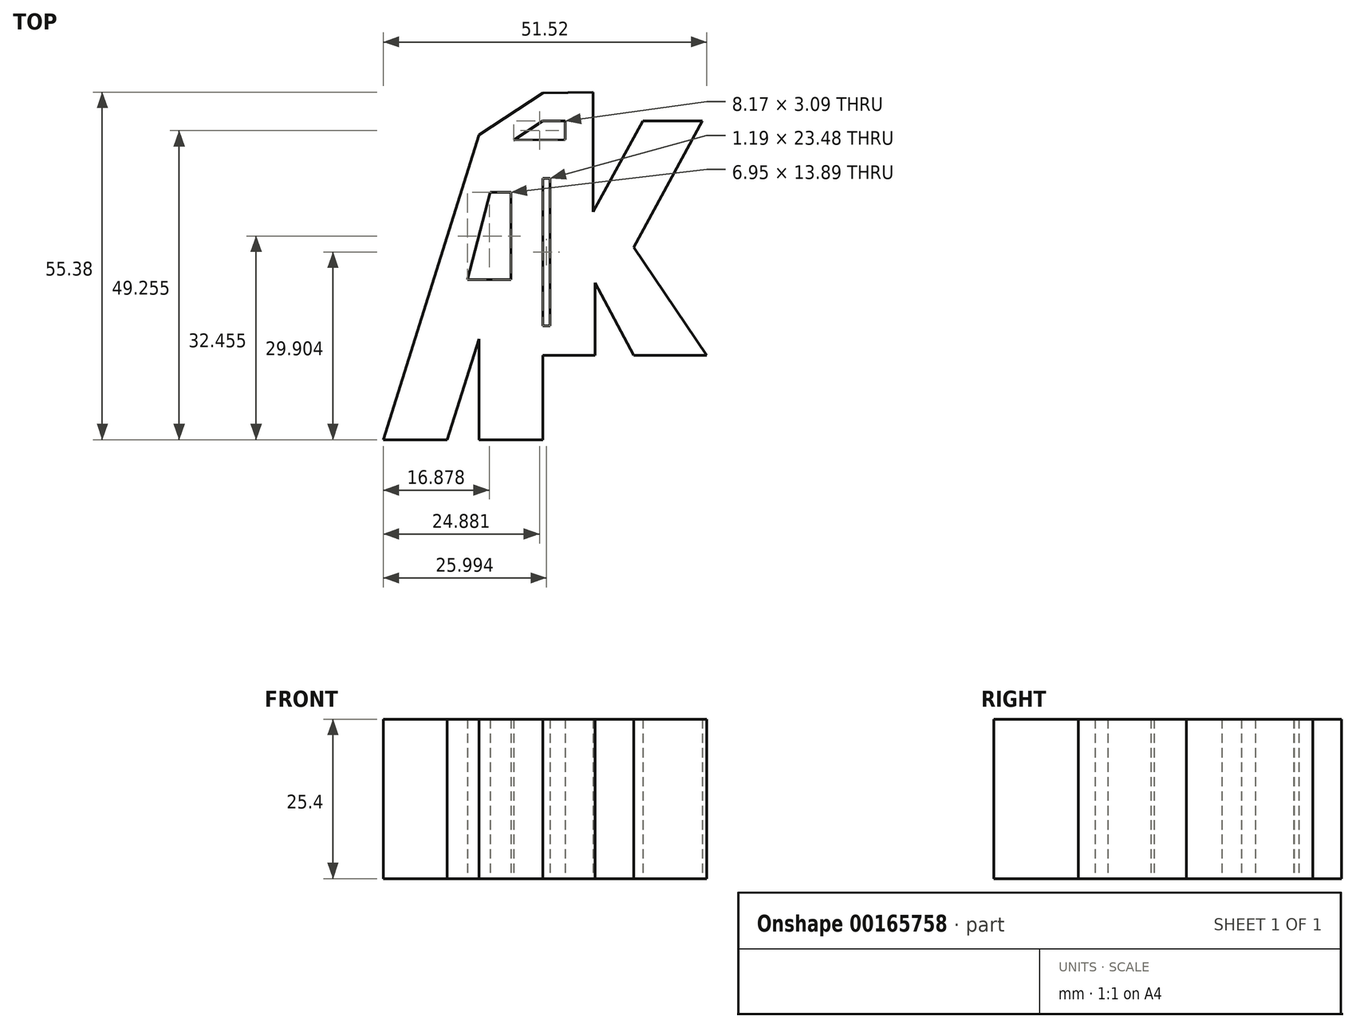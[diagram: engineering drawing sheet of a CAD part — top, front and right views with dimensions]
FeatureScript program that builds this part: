
annotation { "Feature Type Name" : "Feature", "Feature Type Description" : "" }
export const myFeature = defineFeature(function(context is Context, id is Id, definition is map)
    precondition{}
    {
        {
            var Q0;
            Q0=qCreatedBy(makeId("Top.planeOp"),FACE);
            var sketch = newSketch(context, id + "F0", { "sketchPlane" : qUnion([Q0])});
            skLineSegment(sketch, "E0", {"start": v(0, 0) * mm, "end": v(0, 50.8) * mm});
            skLineSegment(sketch, "E1.top", {"start": v(0, 0) * mm, "end": v(-10.16, 0) * mm});
            skLineSegment(sketch, "E1.left", {"start": v(0, 50.8) * mm, "end": v(0, 0) * mm});
            skLineSegment(sketch, "E2", {"start": v(-25.4, 0) * mm, "end": v(-15.24, 0) * mm});
            skLineSegment(sketch, "E3", {"start": v(-10.16, 0) * mm, "end": v(-10.16, 16.08) * mm});
            skLineSegment(sketch, "E4", {"start": v(-10.16, 16.08) * mm, "end": v(-15.24, 0) * mm});
            skLineSegment(sketch, "E5", {"start": v(-8.36, 39.4) * mm, "end": v(-5.05, 39.4) * mm});
            skLineSegment(sketch, "E6", {"start": v(-5.05, 39.4) * mm, "end": v(-5.05, 25.5) * mm});
            skLineSegment(sketch, "E7", {"start": v(-5.05, 25.5) * mm, "end": v(-12, 25.5) * mm});
            skLineSegment(sketch, "E8", {"start": v(-12, 25.5) * mm, "end": v(-8.36, 39.4) * mm});
            skLineSegment(sketch, "E9.trimOffspring", {"start": v(-15.24, 0) * mm, "end": v(-25.4, 0) * mm});
            skLineSegment(sketch, "E10", {"start": v(8.02, 50.8) * mm, "end": v(8.02, 36.3) * mm});
            skLineSegment(sketch, "E11", {"start": v(8.02, 36.3) * mm, "end": v(15.95, 50.8) * mm});
            skLineSegment(sketch, "E12", {"start": v(15.95, 50.8) * mm, "end": v(25.4, 50.8) * mm});
            skLineSegment(sketch, "E13", {"start": v(25.4, 50.8) * mm, "end": v(14.47, 30.64) * mm});
            skLineSegment(sketch, "E14", {"start": v(14.47, 30.64) * mm, "end": v(26.12, 13.44) * mm});
            skLineSegment(sketch, "E15", {"start": v(26.12, 13.44) * mm, "end": v(14.47, 13.44) * mm});
            skLineSegment(sketch, "E16", {"start": v(14.47, 13.44) * mm, "end": v(8.35, 25.01) * mm});
            skLineSegment(sketch, "E17", {"start": v(8.35, 25.01) * mm, "end": v(8.35, 13.44) * mm});
            skLineSegment(sketch, "E18", {"start": v(8.35, 13.44) * mm, "end": v(0, 13.44) * mm});
            skLineSegment(sketch, "E19.bottom", {"start": v(0, 18.16) * mm, "end": v(1.19, 18.16) * mm});
            skLineSegment(sketch, "E19.top", {"start": v(0, 41.65) * mm, "end": v(1.19, 41.65) * mm});
            skLineSegment(sketch, "E19.left", {"start": v(0, 18.16) * mm, "end": v(0, 41.65) * mm});
            skLineSegment(sketch, "E19.right", {"start": v(1.19, 18.16) * mm, "end": v(1.19, 41.65) * mm});
            skLineSegment(sketch, "E20", {"start": v(8.02, 50.8) * mm, "end": v(8.02, 55.38) * mm});
            skLineSegment(sketch, "E21", {"start": v(-10.16, 48.58) * mm, "end": v(0, 55.26) * mm});
            skLineSegment(sketch, "E22", {"start": v(0, 55.26) * mm, "end": v(8.02, 55.38) * mm});
            skLineSegment(sketch, "E23", {"start": v(-4.6, 47.7) * mm, "end": v(0, 50.8) * mm});
            skLineSegment(sketch, "E24", {"start": v(3.57, 50.8) * mm, "end": v(3.57, 47.81) * mm});
            skLineSegment(sketch, "E25", {"start": v(3.57, 47.81) * mm, "end": v(-4.6, 47.7) * mm});
            skLineSegment(sketch, "E26", {"start": v(-10.16, 48.58) * mm, "end": v(-25.4, 0) * mm});
            skLineSegment(sketch, "E27", {"start": v(3.57, 50.8) * mm, "end": v(0, 50.8) * mm});
            skSolve(sketch);
        }
        {
            var Q0;
            {var subQ1=sQuery(id+"F0.wireOp",EDGE,"E1.top");Q0=makeQuery(id+"F0.imprint","IMPRINT",FACE,{"disambiguationData":[TD([[makeQuery(id+"F0.imprint","IMPRINT",EDGE,{"derivedFrom":subQ1}),-1.0]])]});}
            extrude(context, id + "F1", {"entities" : qUnion([Q0]), "depth" : 25.4 * mm});
        }
    });
